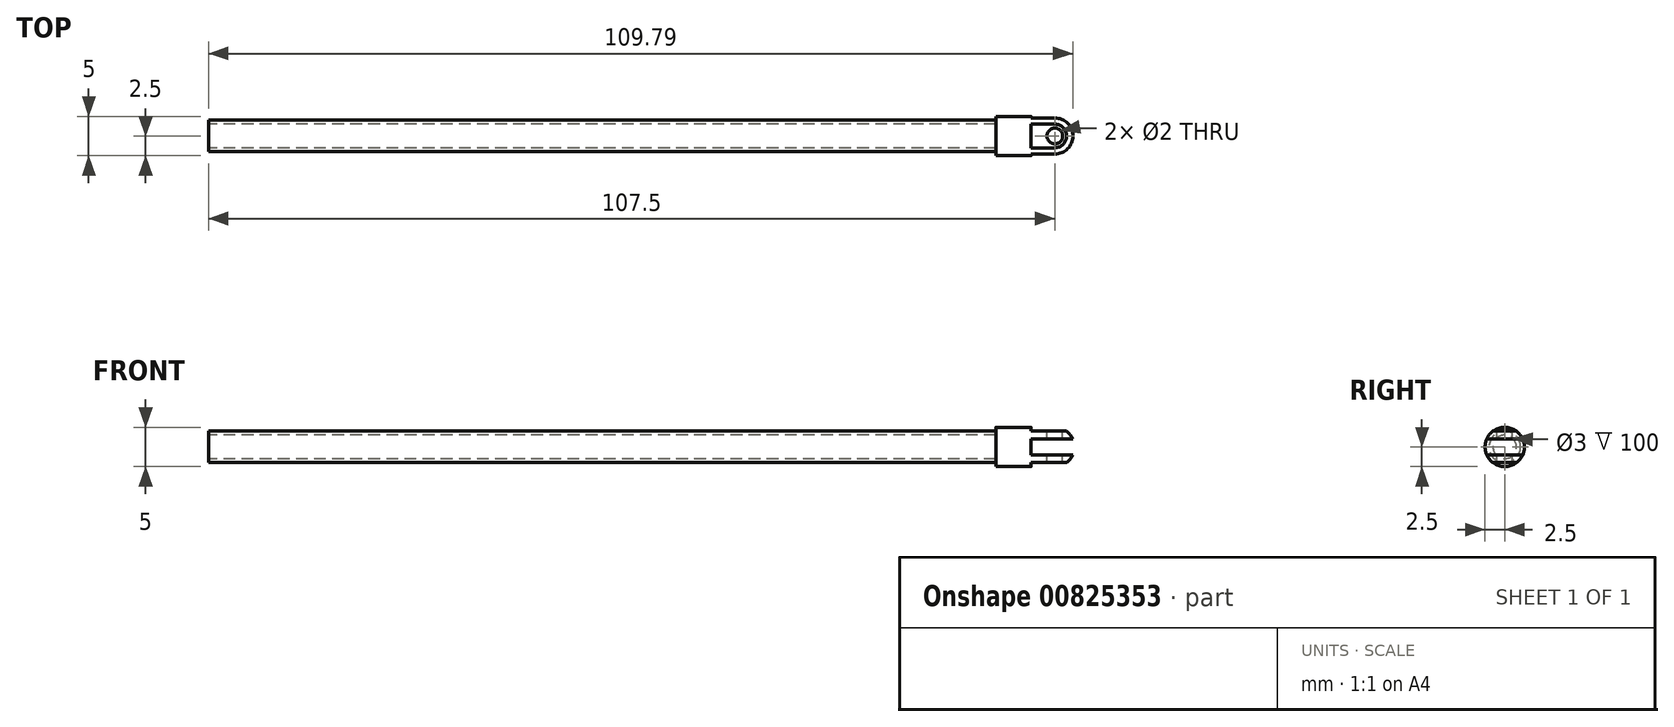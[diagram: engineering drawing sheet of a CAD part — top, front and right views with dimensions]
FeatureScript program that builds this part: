
annotation { "Feature Type Name" : "Feature", "Feature Type Description" : "" }
export const myFeature = defineFeature(function(context is Context, id is Id, definition is map)
    precondition{}
    {
        {
            var Q0;
            Q0=qCreatedBy(makeId("Right.planeOp"),FACE);
            var sketch = newSketch(context, id + "F0", { "sketchPlane" : qUnion([Q0])});
            skCircle(sketch, "E0", {"center": v(0, 0) * mm, "radius": 2 * mm});
            skCircle(sketch, "E1", {"center": v(0, 0) * mm, "radius": 1.5 * mm});
            skSolve(sketch);
        }
        {
            var Q0;
            Q0=makeQuery(id+"F0.imprint","IMPRINT",FACE,{"disambiguationData":[TD([[makeQuery(id+"F0.imprint","IMPRINT",EDGE,{"derivedFrom":sQuery(id+"F0.wireOp",EDGE,"E0")}),1.0]])]});
            extrude(context, id + "F1", {"entities" : qUnion([Q0]), "depth" : 100 * mm, "offsetDistance" : 25 * mm});
        }
        {
            var Q0;
            Q0=makeQuery(id+"F1.opExtrude","CAP_FACE",FACE,{"disambiguationData":[OSD([sQuery(id+"F0.wireOp",EDGE,"E0"),sQuery(id+"F0.wireOp",EDGE,"E1")])],"isStart":false});
            var sketch = newSketch(context, id + "F2", { "sketchPlane" : qUnion([Q0])});
            skCircle(sketch, "E2", {"center": v(0, 0) * mm, "radius": 2.5 * mm});
            skSolve(sketch);
        }
        {
            var Q0;
            Q0=makeQuery(id+"F2.imprint","IMPRINT",FACE,{"disambiguationData":[TD([[makeQuery(id+"F2.imprint","IMPRINT",EDGE,{"derivedFrom":makeQuery(id+"F1.opExtrude","CAP_EDGE",EDGE,{"disambiguationData":[OSD([sQuery(id+"F0.wireOp",EDGE,"E0")])],"isStart":false})}),1.0]])]});
            var Q1;
            Q1=makeQuery(id+"F2.imprint","IMPRINT",FACE,{"disambiguationData":[TD([[makeQuery(id+"F2.imprint","IMPRINT",EDGE,{"derivedFrom":sQuery(id+"F2.wireOp",EDGE,"E2")}),1.0]])]});
            var Q2;
            Q2=makeQuery(id+"F2.imprint","IMPRINT",FACE,{"disambiguationData":[TD([[makeQuery(id+"F2.imprint","IMPRINT",EDGE,{"derivedFrom":makeQuery(id+"F1.opExtrude","CAP_EDGE",EDGE,{"disambiguationData":[OSD([sQuery(id+"F0.wireOp",EDGE,"E1")])],"isStart":false})}),1.0]])]});
            extrude(context, id + "F3", {"entities" : qUnion([Q0, Q1, Q2]), "operationType" : NewBodyOperationType.ADD, "depth" : 10 * mm, "offsetDistance" : 25 * mm});
        }
        {
            var Q0;
            Q0=makeQuery(id+"F3.opExtrude","CAP_EDGE",EDGE,{"disambiguationData":[OSD([sQuery(id+"F2.wireOp",EDGE,"E2")])],"isStart":false});
            fillet(context, id + "F4", {"entities" : qUnion([Q0]), "radius" : 2.5 * mm, "tangentPropagation" : true, "allowEdgeOverflow" : false});
        }
        {
            var Q0;
            Q0=qCreatedBy(makeId("Front.planeOp"),FACE);
            var sketch = newSketch(context, id + "F5", { "sketchPlane" : qUnion([Q0])});
            skLineSegment(sketch, "E3.bottom", {"start": v(104.5, -1) * mm, "end": v(114.5, -1) * mm});
            skLineSegment(sketch, "E3.top", {"start": v(104.5, 1) * mm, "end": v(114.5, 1) * mm});
            skLineSegment(sketch, "E3.left", {"start": v(104.5, -1) * mm, "end": v(104.5, 1) * mm});
            skLineSegment(sketch, "E3.right", {"start": v(114.5, -1) * mm, "end": v(114.5, 1) * mm});
            skPoint(sketch, "E3.middle", {"position": v(109.5, 0) * mm});
            skLineSegment(sketch, "E4.bottom", {"start": v(104.5, 2) * mm, "end": v(114.5, 2) * mm});
            skLineSegment(sketch, "E4.top", {"start": v(104.5, 4) * mm, "end": v(114.5, 4) * mm});
            skLineSegment(sketch, "E4.left", {"start": v(104.5, 2) * mm, "end": v(104.5, 4) * mm});
            skLineSegment(sketch, "E4.right", {"start": v(114.5, 2) * mm, "end": v(114.5, 4) * mm});
            skPoint(sketch, "E4.middle", {"position": v(109.5, 3) * mm});
            skLineSegment(sketch, "E5.bottom", {"start": v(104.5, -4) * mm, "end": v(114.5, -4) * mm});
            skLineSegment(sketch, "E5.top", {"start": v(104.5, -2) * mm, "end": v(114.5, -2) * mm});
            skLineSegment(sketch, "E5.left", {"start": v(104.5, -4) * mm, "end": v(104.5, -2) * mm});
            skLineSegment(sketch, "E5.right", {"start": v(114.5, -4) * mm, "end": v(114.5, -2) * mm});
            skPoint(sketch, "E5.middle", {"position": v(109.5, -3) * mm});
            skSolve(sketch);
        }
        {
            var Q0;
            Q0=makeQuery(id+"F5.imprint","IMPRINT",FACE,{"disambiguationData":[TD([[makeQuery(id+"F5.imprint","IMPRINT",EDGE,{"derivedFrom":sQuery(id+"F5.wireOp",EDGE,"E4.bottom")}),1.0]])]});
            var Q1;
            Q1=makeQuery(id+"F5.imprint","IMPRINT",FACE,{"disambiguationData":[TD([[makeQuery(id+"F5.imprint","IMPRINT",EDGE,{"derivedFrom":sQuery(id+"F5.wireOp",EDGE,"E3.bottom")}),1.0]])]});
            var Q2;
            Q2=makeQuery(id+"F5.imprint","IMPRINT",FACE,{"disambiguationData":[TD([[makeQuery(id+"F5.imprint","IMPRINT",EDGE,{"derivedFrom":sQuery(id+"F5.wireOp",EDGE,"E5.bottom")}),1.0]])]});
            extrude(context, id + "F6", {"entities" : qUnion([Q0, Q1, Q2]), "operationType" : NewBodyOperationType.REMOVE, "endBound" : BoundingType.SYMMETRIC, "oppositeDirection" : true, "depth" : 10 * mm, "offsetDistance" : 25 * mm});
        }
        {
            var Q0;
            Q0=makeQuery(id+"F6.boolean.opBoolean","COPY",FACE,{"derivedFrom":makeQuery(id+"F6.opExtrude","SWEPT_FACE",FACE,{"disambiguationData":[OSD([sQuery(id+"F5.wireOp",EDGE,"E4.bottom")])]})});
            var sketch = newSketch(context, id + "F7", { "sketchPlane" : qUnion([Q0])});
            skCircle(sketch, "E6", {"center": v(107.5, 0) * mm, "radius": 1 * mm});
            skSolve(sketch);
        }
        {
            var Q0;
            Q0=makeQuery(id+"F7.imprint","IMPRINT",FACE,{"disambiguationData":[TD([[makeQuery(id+"F7.imprint","IMPRINT",EDGE,{"derivedFrom":sQuery(id+"F7.wireOp",EDGE,"E6")}),1.0]])]});
            extrude(context, id + "F8", {"entities" : qUnion([Q0]), "operationType" : NewBodyOperationType.REMOVE, "endBound" : BoundingType.THROUGH_ALL, "oppositeDirection" : true, "depth" : 25 * mm, "offsetDistance" : 25 * mm});
        }
    });
